SOLIDWORKS PART (.sldprt)
format: sldprt  version: not decoded by parser v0  size: 142,336 bytes
history: native  units: mm
features: sketch x4, cut_extrude x3, chamfer x2, material x1, extrude x1 (+16 scaffold rows collapsed)
feature tree (27):
  scaffold x16  (default folders/planes/origin — collapsed)
  material  "Plain Carbon Steel"
  sketch  "Sketch1"
  extrude  "Boss-Extrude1"  [1 undecoded]
  chamfer  "Chamfer1"  Distance=10mm Angle=45deg
  chamfer  "Chamfer2"  Distance=1mm Angle=45deg
  sketch  "Sketch2"  dims[D1=3.4mm]
  cut_extrude  "Cut-Extrude1"  [1 undecoded]
  sketch  "Sketch3"  dims[D1=2.2mm D2=6.0mm]
  cut_extrude  "Cut-Extrude2"  [1 undecoded]
  sketch  "Sketch4"  dims[D1=6.35mm]
  cut_extrude  "Cut-Extrude3"  Depth=3mm
decode coverage: 6 of 10 modeling features carry decoded parameters
note: 3 parameter values undecoded
summary: no parameter record found for 3 features
note: suppression state not decoded; provenance and decode notes live in map.json
